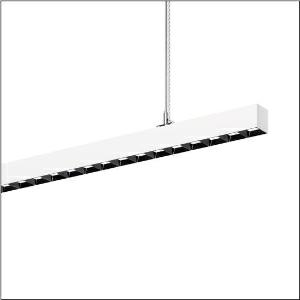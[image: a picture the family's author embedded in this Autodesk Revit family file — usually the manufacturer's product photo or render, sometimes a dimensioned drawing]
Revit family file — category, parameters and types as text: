
# Revit family: silica_r__21_51mx31tat7w_6f20
name_source: partatom
category: Lighting Fixtures
units: mm (PartAtom-declared; Revit-internal decimal feet)

## family parameters
Cut with Voids When Loaded = No
Host = Face
Light Source = No
Part Type = Normal
Room Calculation Point = No
Round Connector Dimension = Use Diameter
Shared = No

## types (1)
- --- (1 x LED, 6220 lm, 53.5 W, 6500K)
    Apparent Load = 54 VA
    CIE Flux Codes = 85 99 100 60 100
    Color Rendering = 80
    Color Temperature = 6500K
    Default Elevation = 1800 mm
    Description = Silica® 21, office luminaire, primary light control with darklight reflector, of PMMA, black, CAT 2 (L<= 3000cd/m²), light emission: direct/indirect distribution, primary light characteristic: symmetric, installation type: suspended mounting, LED, rated luminous flux: 6.220lm, luminous efficacy: 111lm/W, light colour: 8tw, colour temperature: 2700..6500K, control gear: ECG DALI, with terminal, 3+2-pole, max. 2.5mm², mains connection: 220..240V, AC, 50/60Hz, rated input power: 56.2W, luminaire housing, of aluminium, traffic white (RAL 9016), length: 1.204mm, width: 53mm, height: 53mm, protection rating (complete): IP20, insulation class (complete): insulation class I (protective earthing), certification: CE, permissible operating ambient temperature: 0..+35°C, standard: EN 50419, packaging unit: 1 piece
    Height = 53 mm
    Lamp = 1 x LED
    Lamp Light Flux = 6220 lm
    Lamp Power = 53.5 W
    Lamp count = 1
    Length = 1204 mm
    Luminous efficacy = 116 lm/W
    Manufacturer = Siteco
    ModVariant = No
    Model = 51MX31TAT7W
    Mounting Place = Ceiling
    Mounting Type = Pendant
    Number of Poles = 1
    OnlyDefault = Yes
    Power Factor = 1
    Product Name = Silica® 21
    Product group = office luminaire | ceiling pendant
    ProductGroupID = 902
    Protection Class = Protection class I
    Protection Degree = IP 20
    RLX_Detail_Level = 1
    RLX_Emergency_Light_Flux = 0 lm
    RLX_Emergency_Type = 0
    RLX_Emergency_Type_DB = No
    RlxData = <blob elided: 40409 chars, md5=a46dc482>
    Socket = socket
    Standby Power = 0 W
    System Light Flux = 6220 lm
    System Power = 54 W
    Type Comments = individual setting
    Type Image = l_1313619.jpg
    URL = http://relux.com
    VarID = @adj_089277
    Voltage = 0 V
    Weight = 0.00 kg
    Width = 53 mm

## geometry (parser evidence)
native form markers: Blend x4, Sweep x11
no freeform markers — native parametric forms only
